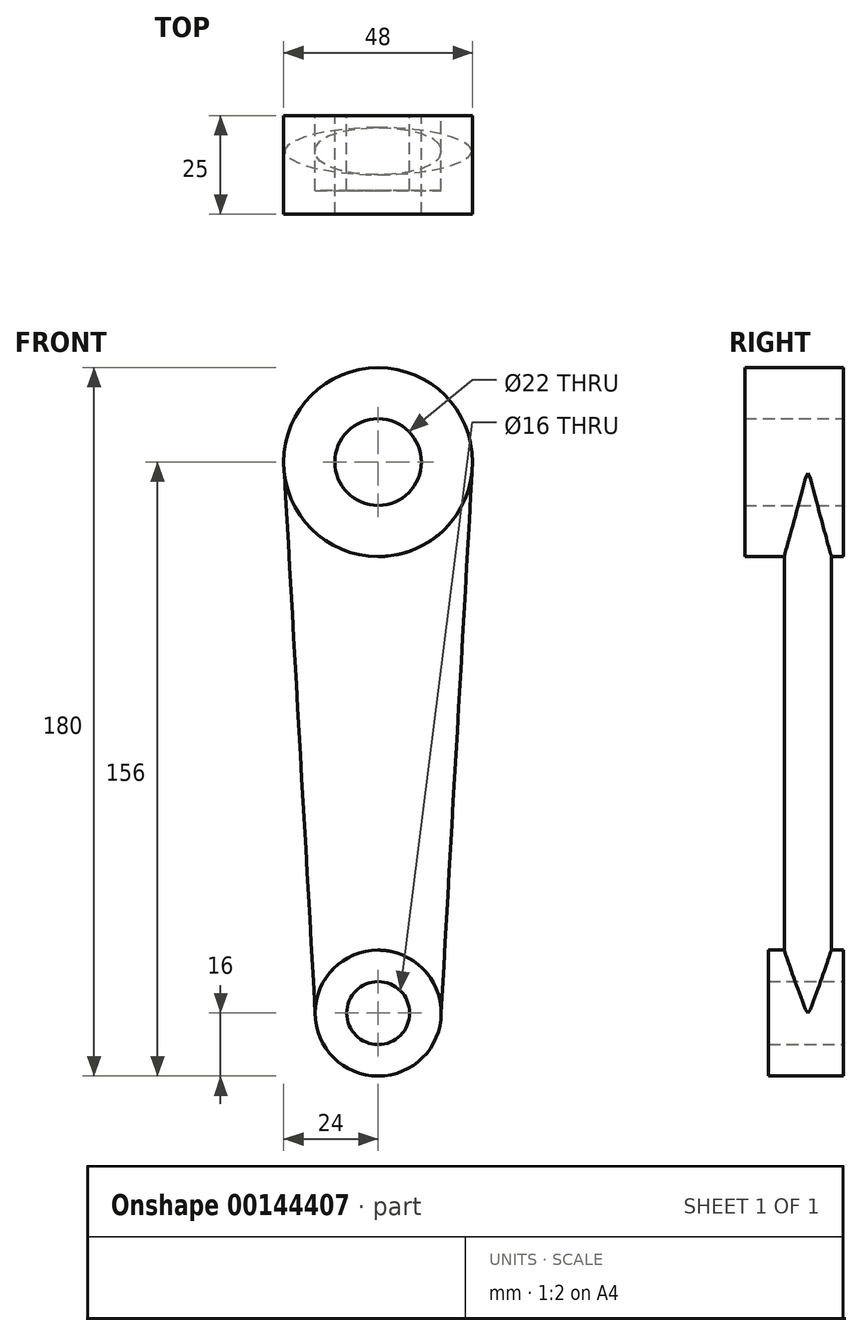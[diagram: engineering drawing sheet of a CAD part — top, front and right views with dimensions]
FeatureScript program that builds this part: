
annotation { "Feature Type Name" : "Feature", "Feature Type Description" : "" }
export const myFeature = defineFeature(function(context is Context, id is Id, definition is map)
    precondition{}
    {
        {
            var Q0;
            Q0=qCreatedBy(makeId("Front.planeOp"),FACE);
            var sketch = newSketch(context, id + "F0", { "sketchPlane" : qUnion([Q0])});
            skCircle(sketch, "E0", {"center": v(0, 0) * mm, "radius": 8 * mm});
            skCircle(sketch, "E1", {"center": v(0, 0) * mm, "radius": 16 * mm});
            skCircle(sketch, "E2", {"center": v(0, 140) * mm, "radius": 11 * mm});
            skCircle(sketch, "E3", {"center": v(0, 140) * mm, "radius": 24 * mm});
            skSolve(sketch);
        }
        {
            var Q0;
            Q0=makeQuery(id+"F0.imprint","IMPRINT",FACE,{"disambiguationData":[TD([[makeQuery(id+"F0.imprint","IMPRINT",EDGE,{"derivedFrom":sQuery(id+"F0.wireOp",EDGE,"E0")}),-1.0]])]});
            var Q1;
            Q1=makeQuery(id+"F0.imprint","IMPRINT",FACE,{"disambiguationData":[TD([[makeQuery(id+"F0.imprint","IMPRINT",EDGE,{"derivedFrom":sQuery(id+"F0.wireOp",EDGE,"E0")}),1.0]])]});
            extrude(context, id + "F1", {"entities" : qUnion([Q0, Q1]), "depth" : 19 * mm});
        }
        {
            var Q0;
            Q0=makeQuery(id+"F0.imprint","IMPRINT",FACE,{"disambiguationData":[TD([[makeQuery(id+"F0.imprint","IMPRINT",EDGE,{"derivedFrom":sQuery(id+"F0.wireOp",EDGE,"E2")}),-1.0]])]});
            var Q1;
            Q1=makeQuery(id+"F0.imprint","IMPRINT",FACE,{"disambiguationData":[TD([[makeQuery(id+"F0.imprint","IMPRINT",EDGE,{"derivedFrom":sQuery(id+"F0.wireOp",EDGE,"E2")}),1.0]])]});
            extrude(context, id + "F2", {"entities" : qUnion([Q0, Q1]), "depth" : 25 * mm});
        }
        {
            var Q0;
            Q0=qCreatedBy(makeId("Top.planeOp"),FACE);
            var sketch = newSketch(context, id + "F3", { "sketchPlane" : qUnion([Q0])});
            skEllipse(sketch, "E4", {"center": v(0, -9) * mm, "majorRadius": 16 * mm, "minorRadius": 6 * mm, "majorAxis": v(1, 0)});
            skPoint(sketch, "E5", {"position": v(0, -3) * mm});
            skLineSegment(sketch, "E6", {"start": v(16, 0) * mm, "end": v(16, -19) * mm, "construction": true});
            skSolve(sketch);
        }
        {
            var Q0;
            Q0=sQuery(id+"F0.wireOp",VERTEX,"E3.center");
            var Q1;
            Q1=qCreatedBy(makeId("Top.planeOp"),FACE);
            cPlane(context, id + "F4", {"entities" : qUnion([Q0, Q1]), "cplaneType" : CPlaneType.PLANE_POINT, "offset" : 25 * mm, "width" : 150 * mm, "height" : 150 * mm});
        }
        {
            var Q0;
            Q0=qCreatedBy(id+"F4.planeOp",FACE);
            var sketch = newSketch(context, id + "F5", { "sketchPlane" : qUnion([Q0])});
            skEllipse(sketch, "E7", {"center": v(0, -9) * mm, "majorRadius": 24 * mm, "minorRadius": 6 * mm, "majorAxis": v(1, 0)});
            skPoint(sketch, "E8", {"position": v(0, -3) * mm});
            skLineSegment(sketch, "E9", {"start": v(24, 0) * mm, "end": v(24, -25) * mm, "construction": true});
            skSolve(sketch);
        }
        {
            var Q0;
            Q0=makeQuery(id+"F5.imprint","IMPRINT",FACE,{"disambiguationData":[TD([[makeQuery(id+"F5.imprint","IMPRINT",EDGE,{"derivedFrom":sQuery(id+"F5.wireOp",EDGE,"E7")}),1.0]])]});
            var Q1;
            Q1=makeQuery(id+"F3.imprint","IMPRINT",FACE,{"disambiguationData":[TD([[makeQuery(id+"F3.imprint","IMPRINT",EDGE,{"derivedFrom":sQuery(id+"F3.wireOp",EDGE,"E4")}),1.0]])]});
            loft(context, id + "F6", {"operationType" : NewBodyOperationType.ADD, "sheetProfilesArray" : [{ "sheetProfileEntities" : qUnion([Q0]) }, { "sheetProfileEntities" : qUnion([Q1]) }]});
        }
        {
            var Q0;
            Q0=makeQuery(id+"F0.imprint","IMPRINT",FACE,{"disambiguationData":[TD([[makeQuery(id+"F0.imprint","IMPRINT",EDGE,{"derivedFrom":sQuery(id+"F0.wireOp",EDGE,"E2")}),1.0]])]});
            var Q1;
            Q1=makeQuery(id+"F0.imprint","IMPRINT",FACE,{"disambiguationData":[TD([[makeQuery(id+"F0.imprint","IMPRINT",EDGE,{"derivedFrom":sQuery(id+"F0.wireOp",EDGE,"E0")}),1.0]])]});
            extrude(context, id + "F7", {"entities" : qUnion([Q0, Q1]), "operationType" : NewBodyOperationType.REMOVE, "endBound" : BoundingType.THROUGH_ALL, "depth" : 25 * mm});
        }
    });
